# Revit family: QF_Dietatec_GENIER-150-CH5-FS
name_source: partatom
category: Specialty Equipment
revit_build: Autodesk Revit 2016 (Build: 20150220_1215(x64)
units: mm (PartAtom-declared; Revit-internal decimal feet)

## family parameters
Always vertical = Yes
Cut with Voids When Loaded = No
OmniClass Number = 23.40.40.14
OmniClass Title = Food Service Equipment
Part Type = Normal
Room Calculation Point = No
Round Connector Dimension = Use Diameter
Shared = No
Work Plane-Based = No

## types (2) — shared parameters
Accessory = No
Apparent Power = 28500 VA
Assembly Code = E1090320
BTUH = 0 W
Cold Water Flow = 0.0 L/s
Cold Water Size = 13 mm
Cold Water Temperature Recommended = 0 °C
Conn Conduit = No
Cycle = 50 Hz
Depth Actual = 1274 mm  [stored 4.17979 ft]
Electric power = 28500 W
FL Amps = 41 A
Height Actual = 1080 mm  [stored 3.54331 ft]
Length Actual = 1430 mm  [stored 4.6916 ft]
Manufacturer = DIETATEC
Max Overcurrent Protection = 0 A
Min Ckt Ampacity = 0 A
Model = GENIER ACE 150 CH5 FS
Number of Poles = 3
Phase = 3
Refrigerant Volume = 0.0 L/s
Refrigeration Evaporation Temperature = 0 °C
Refrigeration Liquid Line Size = 25 mm  [stored 0.082021 ft]
Refrigeration Suction Line Size = 25 mm  [stored 0.082021 ft]
URL = www.dietatec.com
Volts = 400 V
Weight = 320.00 kg
zero-valued in all types: Cost

## per-type parameters (varying)
| type | Description |
| 58015-56654 | GENIER ACE CIRCULATED CHILLING MIXER KETTLE WITH INTEGRATED RETURN PUMP, AUX LEG FAN AND INSULATED CHILL LINE COMPONENTS, 150L |
| 58015-50354 | GENIER ACE CIRCULATED CHILLING MIXER KETTLE WITH INTEGRATED RETURN PUMP, 150L |

note: [stored X ft] marks values corroborated as IEEE doubles in the binary element streams (Revit-internal decimal feet)

## geometry (parser evidence)
native form markers: Sweep x4
no freeform markers — native parametric forms only
